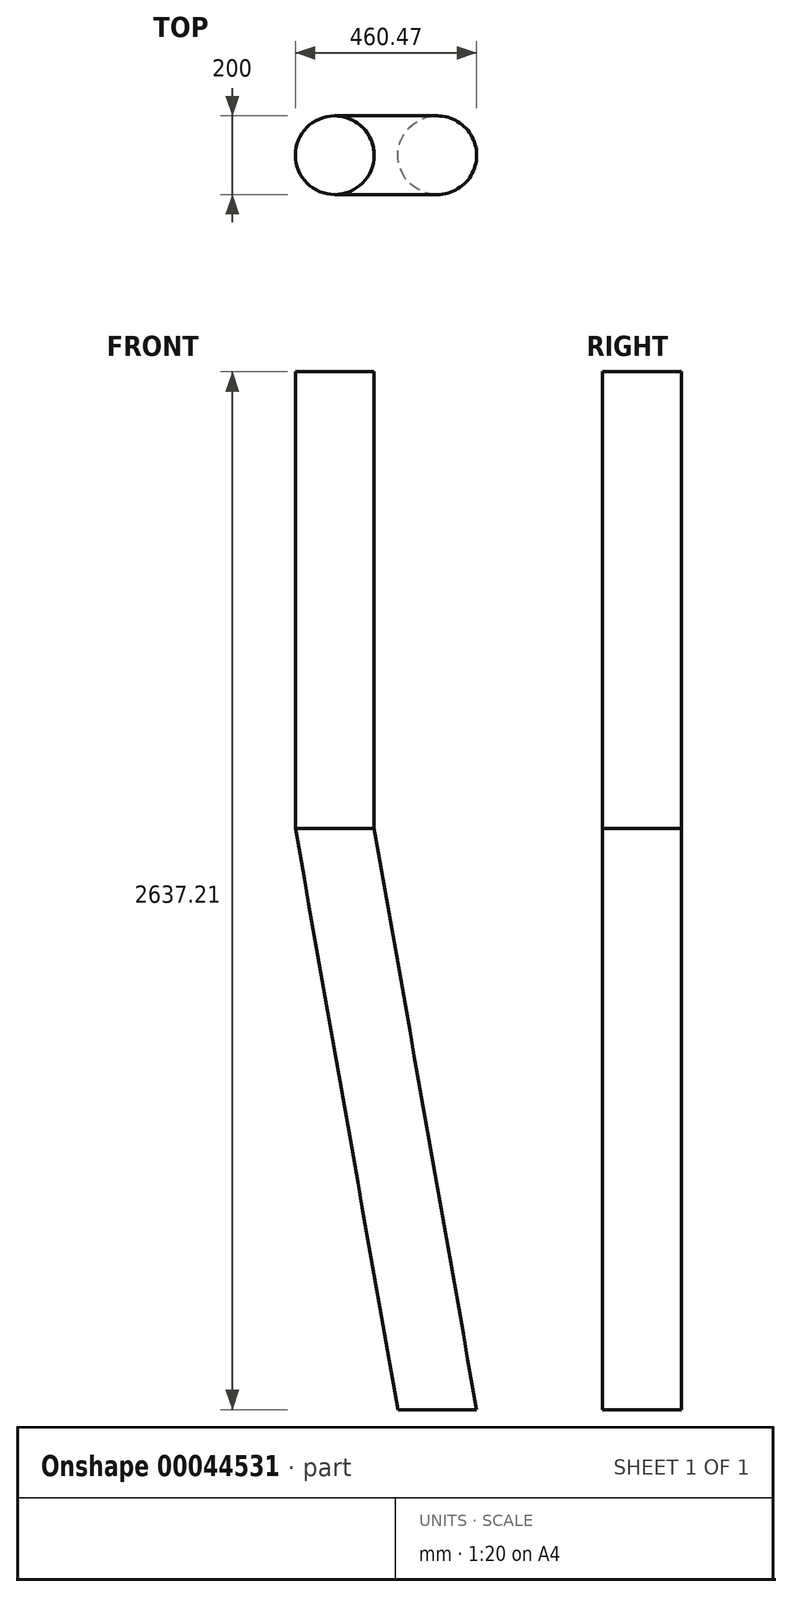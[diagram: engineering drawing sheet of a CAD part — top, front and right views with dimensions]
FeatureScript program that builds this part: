
annotation { "Feature Type Name" : "Feature", "Feature Type Description" : "" }
export const myFeature = defineFeature(function(context is Context, id is Id, definition is map)
    precondition{}
    {
        {
            var Q0;
            Q0=qCreatedBy(makeId("Top.planeOp"),FACE);
            var sketch = newSketch(context, id + "F0", { "sketchPlane" : qUnion([Q0])});
            skCircle(sketch, "E0", {"center": v(0, 0) * mm, "radius": 100 * mm});
            skSolve(sketch);
        }
        {
            var Q0;
            Q0=qCreatedBy(makeId("Front.planeOp"),FACE);
            var sketch = newSketch(context, id + "F1", { "sketchPlane" : qUnion([Q0])});
            skLineSegment(sketch, "E1", {"start": v(0, 0) * mm, "end": v(0, -1160) * mm});
            skLineSegment(sketch, "E2", {"start": v(0, -1160) * mm, "end": v(260.47, -2637.21) * mm});
            skSolve(sketch);
        }
        {
            var Q0;
            Q0=makeQuery(id+"F0.imprint","IMPRINT",FACE,{"disambiguationData":[TD([[makeQuery(id+"F0.imprint","IMPRINT",EDGE,{"derivedFrom":sQuery(id+"F0.wireOp",EDGE,"E0")}),1.0]])]});
            var Q1;
            Q1=sQuery(id+"F0.wireOp",EDGE,"E0");
            extrude(context, id + "F2", {"entities" : qUnion([Q0]), "surfaceEntities" : qUnion([Q1]), "oppositeDirection" : true, "depth" : 1160 * mm});
        }
        {
            var Q0;
            Q0=makeQuery(id+"F2.opExtrude","CAP_FACE",FACE,{"disambiguationData":[OSD([sQuery(id+"F0.wireOp",EDGE,"E0")])],"isStart":false});
            var Q1;
            Q1=sQuery(id+"F1.wireOp",EDGE,"E2");
            sweep(context, id + "F3", {"operationType" : NewBodyOperationType.ADD, "profiles" : qUnion([Q0]), "path" : qUnion([Q1])});
        }
    });
